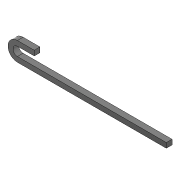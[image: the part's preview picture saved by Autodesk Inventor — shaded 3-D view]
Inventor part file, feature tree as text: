
AUTODESK INVENTOR PART (.ipt)
format: ipt  version: 2020 (Build 240168000, 168)  size: 87,552 bytes
history: native  units: mm
features: extrude x1, sketch x1
ambient origin geometry x8: Origin, YZ Plane, XZ Plane, XY Plane, X Axis, Y Axis, Z Axis, Center Point
bodies: Solid1 (feature_tree)
feature tree (2):
  extrude  "Extrusion1"  Depth=20.0mm
  sketch  "Sketch1"  dims[d0=76.0mm d1=20.0mm d2=20.0mm d4=600.0mm d5=23.0mm d6=0.0mm d7=68.0mm]
